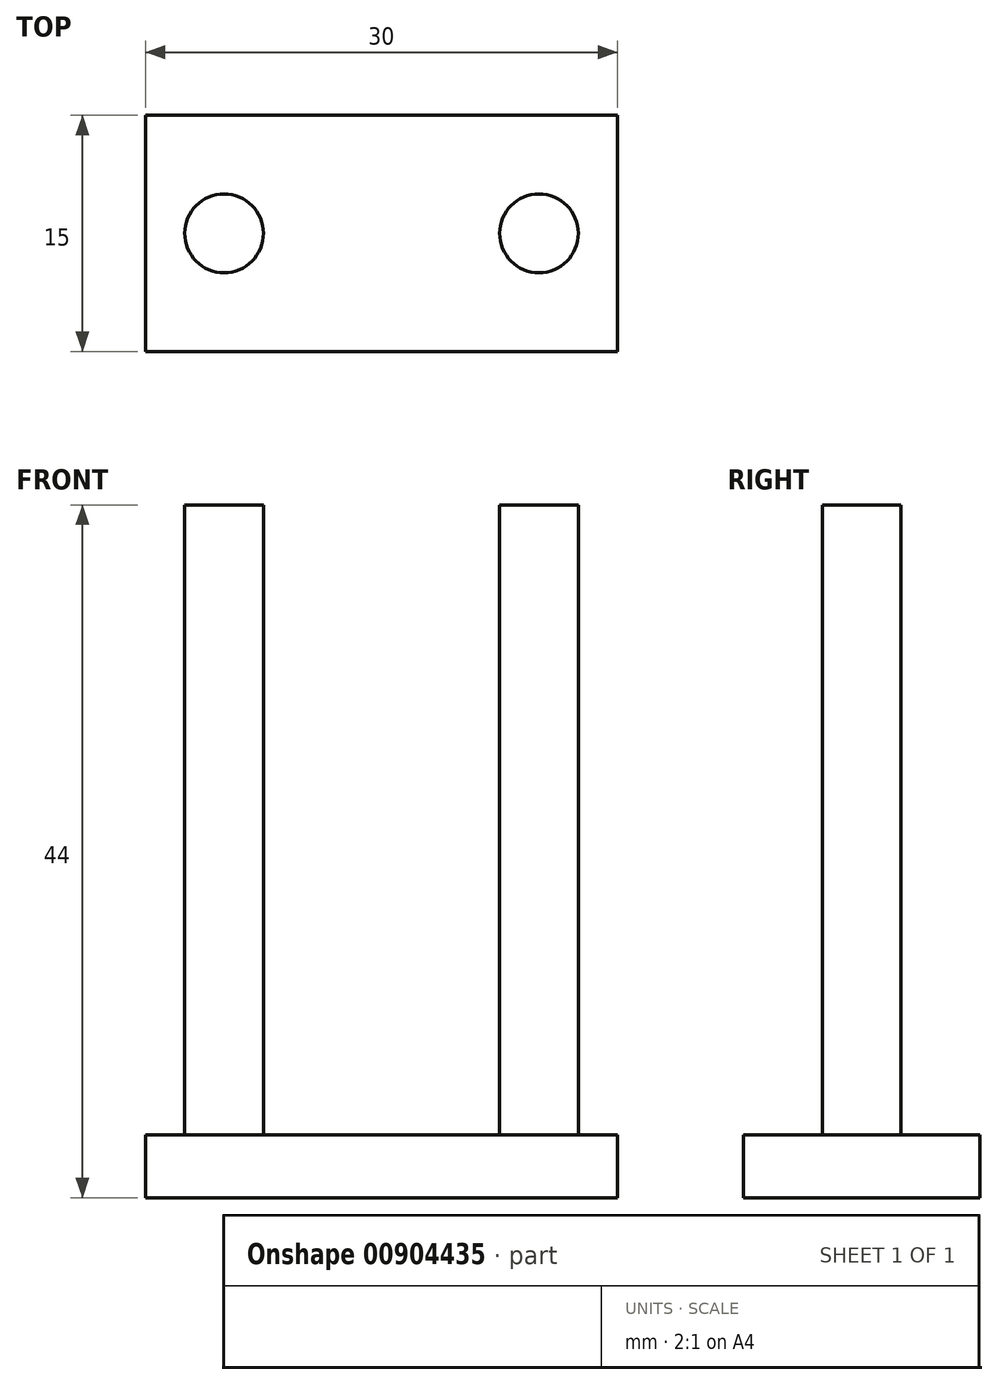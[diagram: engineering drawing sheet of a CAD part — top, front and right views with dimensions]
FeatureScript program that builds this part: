
annotation { "Feature Type Name" : "Feature", "Feature Type Description" : "" }
export const myFeature = defineFeature(function(context is Context, id is Id, definition is map)
    precondition{}
    {
        {
            var Q0;
            Q0=qCreatedBy(makeId("Top.planeOp"),FACE);
            var sketch = newSketch(context, id + "F0", { "sketchPlane" : qUnion([Q0])});
            skLineSegment(sketch, "E0.bottom", {"start": v(0, 0) * mm, "end": v(-30, 0) * mm});
            skLineSegment(sketch, "E0.top", {"start": v(0, 15) * mm, "end": v(-30, 15) * mm});
            skLineSegment(sketch, "E0.left", {"start": v(0, 0) * mm, "end": v(0, 15) * mm});
            skLineSegment(sketch, "E0.right", {"start": v(-30, 0) * mm, "end": v(-30, 15) * mm});
            skPoint(sketch, "E1.centerSnap0", {"position": v(-30, 7.5) * mm});
            skSolve(sketch);
        }
        {
            var Q0;
            Q0=makeQuery(id+"F0.imprint","IMPRINT",FACE,{"disambiguationData":[TD([[makeQuery(id+"F0.imprint","IMPRINT",EDGE,{"derivedFrom":sQuery(id+"F0.wireOp",EDGE,"E0.bottom")}),-1.0]])]});
            extrude(context, id + "F1", {"entities" : qUnion([Q0]), "depth" : 4 * mm, "offsetDistance" : 25 * mm});
        }
        {
            var Q0;
            Q0=makeQuery(id+"F1.opExtrude","CAP_FACE",FACE,{"disambiguationData":[OSD([sQuery(id+"F0.wireOp",EDGE,"E0.bottom"),sQuery(id+"F0.wireOp",EDGE,"E0.top"),sQuery(id+"F0.wireOp",EDGE,"E0.left"),sQuery(id+"F0.wireOp",EDGE,"E0.right")])],"isStart":false});
            var sketch = newSketch(context, id + "F2", { "sketchPlane" : qUnion([Q0])});
            skCircle(sketch, "E2", {"center": v(-25, 7.5) * mm, "radius": 2.5 * mm});
            skCircle(sketch, "E3", {"center": v(-5, 7.5) * mm, "radius": 2.5 * mm});
            skSolve(sketch);
        }
        {
            var Q0;
            Q0=makeQuery(id+"F2.imprint","IMPRINT",FACE,{"disambiguationData":[TD([[makeQuery(id+"F2.imprint","IMPRINT",EDGE,{"derivedFrom":sQuery(id+"F2.wireOp",EDGE,"E2")}),1.0]])]});
            var Q1;
            Q1=makeQuery(id+"F2.imprint","IMPRINT",FACE,{"disambiguationData":[TD([[makeQuery(id+"F2.imprint","IMPRINT",EDGE,{"derivedFrom":sQuery(id+"F2.wireOp",EDGE,"E3")}),1.0]])]});
            extrude(context, id + "F3", {"entities" : qUnion([Q0, Q1]), "operationType" : NewBodyOperationType.ADD, "depth" : 40 * mm, "offsetDistance" : 25 * mm});
        }
    });
